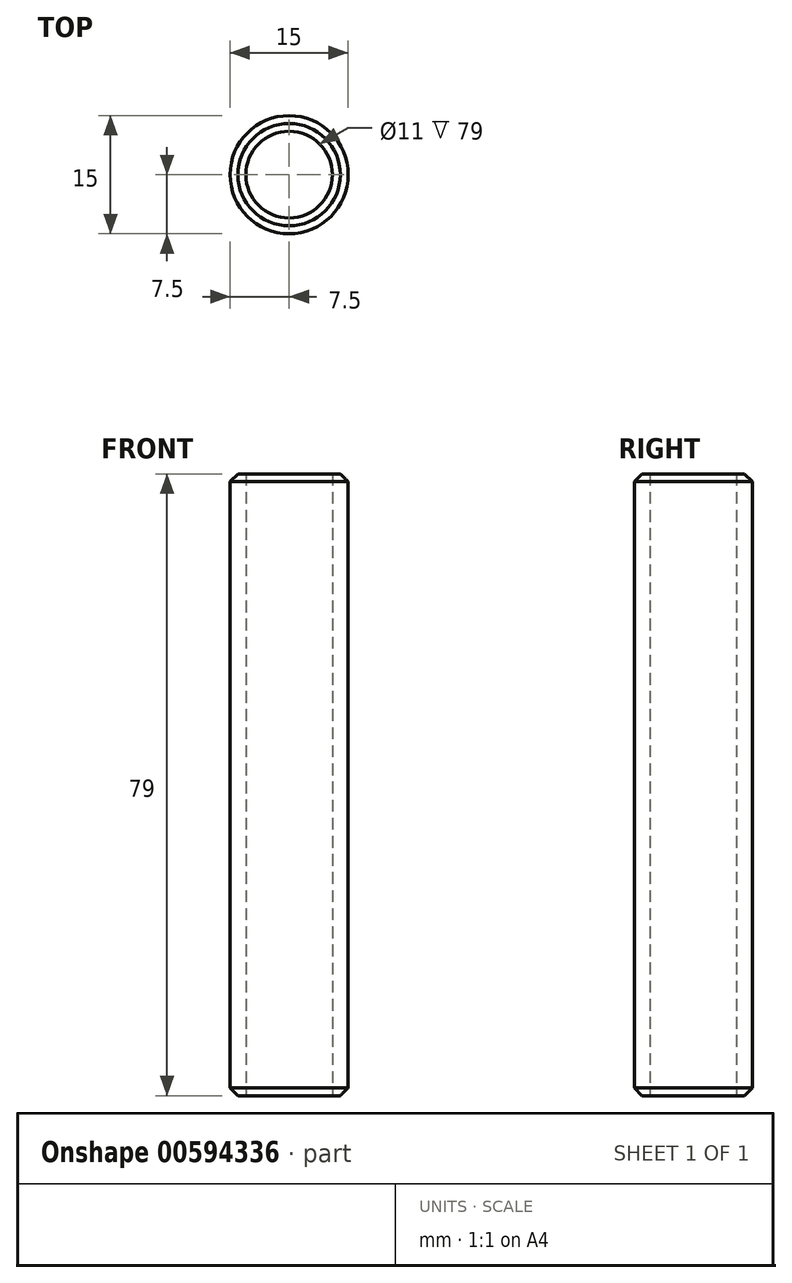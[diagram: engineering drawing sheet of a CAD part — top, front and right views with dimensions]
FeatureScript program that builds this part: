
annotation { "Feature Type Name" : "Feature", "Feature Type Description" : "" }
export const myFeature = defineFeature(function(context is Context, id is Id, definition is map)
    precondition{}
    {
        {
            var Q0;
            Q0=qCreatedBy(makeId("Top.planeOp"),FACE);
            var sketch = newSketch(context, id + "F0", { "sketchPlane" : qUnion([Q0])});
            skCircle(sketch, "E0", {"center": v(0, 0) * mm, "radius": 7.5 * mm});
            skSolve(sketch);
        }
        {
            var Q0;
            Q0 = qSketchRegion(id + "F0", true);
            extrude(context, id + "F1", {"entities" : qUnion([Q0]), "depth" : 79 * mm, "offsetDistance" : 25.4 * mm});
        }
        {
            var Q0;
            Q0=makeQuery(id+"F1.opExtrude","CAP_FACE",FACE,{"disambiguationData":[OSD([sQuery(id+"F0.wireOp",EDGE,"E0")])],"isStart":false});
            var Q1;
            Q1=makeQuery(id+"F1.opExtrude","CAP_FACE",FACE,{"disambiguationData":[OSD([sQuery(id+"F0.wireOp",EDGE,"E0")])],"isStart":true});
            shell(context, id + "F2", {"entities" : qUnion([Q0, Q1]), "thickness" : 2 * mm});
        }
        {
            var Q0;
            Q0=makeQuery(id+"F1.opExtrude","CAP_EDGE",EDGE,{"disambiguationData":[OSD([sQuery(id+"F0.wireOp",EDGE,"E0")])],"isStart":true});
            var Q1;
            Q1=makeQuery(id+"F1.opExtrude","CAP_EDGE",EDGE,{"disambiguationData":[OSD([sQuery(id+"F0.wireOp",EDGE,"E0")])],"isStart":false});
            chamfer(context, id + "F3", {"entities" : qUnion([Q0, Q1]), "width" : 1 * mm, "tangentPropagation" : true});
        }
    });
